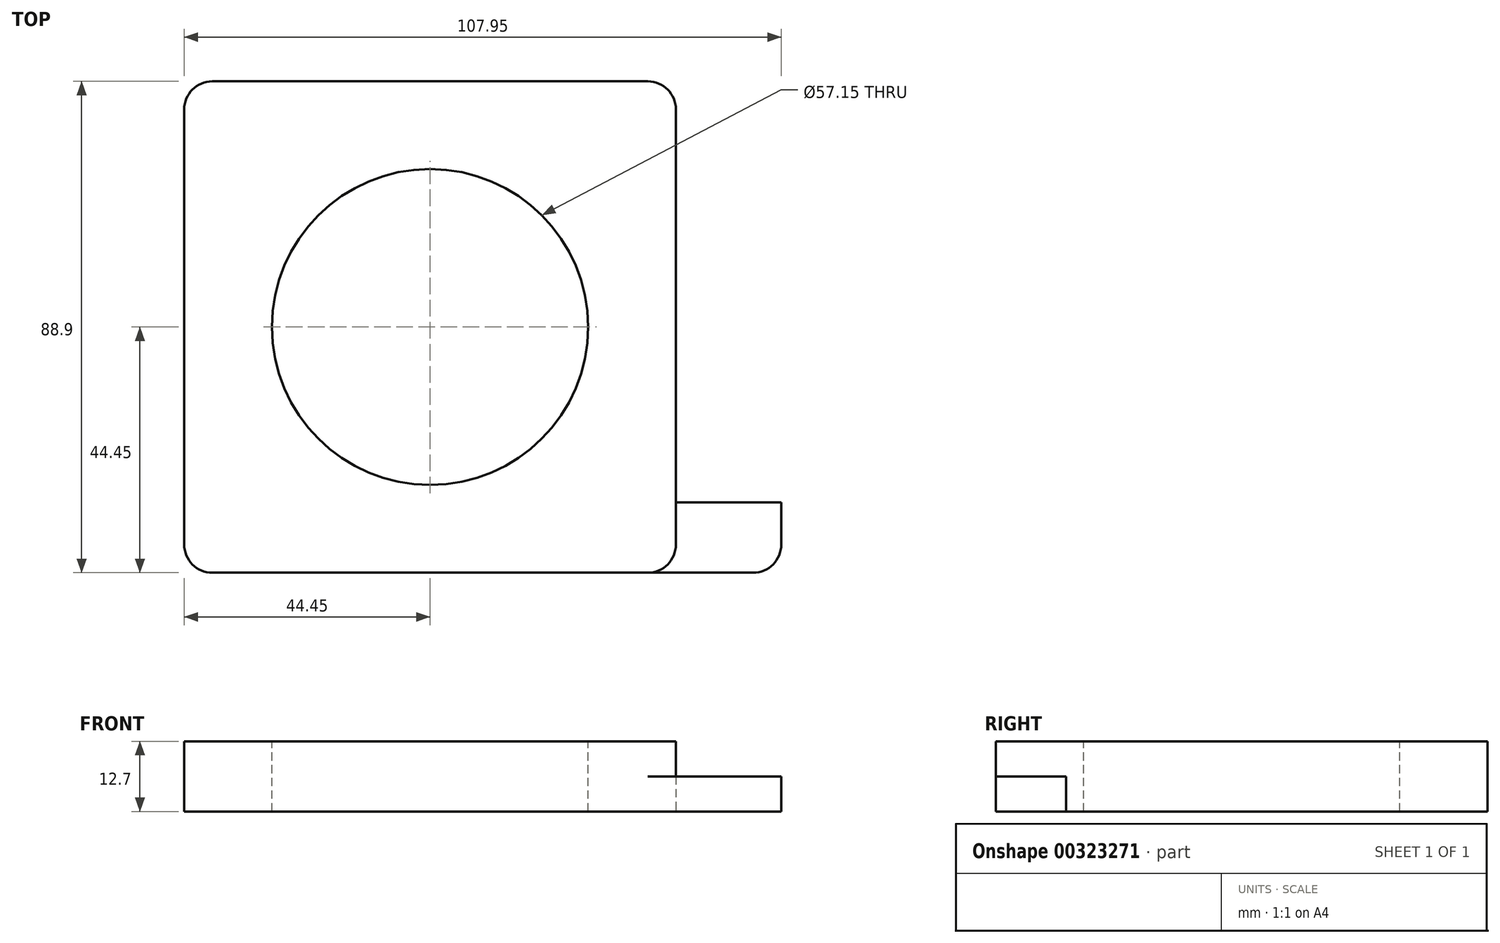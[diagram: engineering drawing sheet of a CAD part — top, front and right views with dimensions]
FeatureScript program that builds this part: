
annotation { "Feature Type Name" : "Feature", "Feature Type Description" : "" }
export const myFeature = defineFeature(function(context is Context, id is Id, definition is map)
    precondition{}
    {
        {
            var Q0;
            Q0=qCreatedBy(makeId("Top.planeOp"),FACE);
            var sketch = newSketch(context, id + "F0", { "sketchPlane" : qUnion([Q0])});
            skLineSegment(sketch, "E0.bottom", {"start": v(-44.45, 44.45) * mm, "end": v(44.45, 44.45) * mm});
            skLineSegment(sketch, "E0.top", {"start": v(-44.45, -44.45) * mm, "end": v(44.45, -44.45) * mm});
            skLineSegment(sketch, "E0.left", {"start": v(-44.45, 44.45) * mm, "end": v(-44.45, -44.45) * mm});
            skLineSegment(sketch, "E0.right", {"start": v(44.45, 44.45) * mm, "end": v(44.45, -44.45) * mm});
            skPoint(sketch, "E0.middle", {"position": v(0, 0) * mm});
            skLineSegment(sketch, "E1.bottom", {"start": v(44.45, -44.45) * mm, "end": v(63.5, -44.45) * mm});
            skLineSegment(sketch, "E1.top", {"start": v(44.45, -31.75) * mm, "end": v(63.5, -31.75) * mm});
            skLineSegment(sketch, "E1.left", {"start": v(44.45, -44.45) * mm, "end": v(44.45, -31.75) * mm});
            skLineSegment(sketch, "E1.right", {"start": v(63.5, -44.45) * mm, "end": v(63.5, -31.75) * mm});
            skSolve(sketch);
        }
        {
            var Q0;
            Q0=makeQuery(id+"F0.imprint","IMPRINT",FACE,{"disambiguationData":[TD([[makeQuery(id+"F0.imprint","IMPRINT",EDGE,{"derivedFrom":sQuery(id+"F0.wireOp",EDGE,"E0.bottom")}),-1.0]])]});
            extrude(context, id + "F1", {"entities" : qUnion([Q0]), "depth" : 12.7 * mm});
        }
        {
            var Q0;
            Q0=makeQuery(id+"F0.imprint","IMPRINT",FACE,{"disambiguationData":[TD([[makeQuery(id+"F0.imprint","IMPRINT",EDGE,{"derivedFrom":sQuery(id+"F0.wireOp",EDGE,"E1.bottom")}),1.0]])]});
            extrude(context, id + "F2", {"entities" : qUnion([Q0]), "operationType" : NewBodyOperationType.ADD, "depth" : 6.35 * mm});
        }
        {
            var Q0;
            Q0=makeQuery(id+"F1.opExtrude","SWEPT_EDGE",EDGE,{"disambiguationData":[OSD([sQuery(id+"F0.wireOp",EDGE,"E0.top"),sQuery(id+"F0.wireOp",EDGE,"E0.left")])]});
            var Q1;
            Q1=makeQuery(id+"F1.opExtrude","SWEPT_EDGE",EDGE,{"disambiguationData":[OSD([sQuery(id+"F0.wireOp",EDGE,"E0.bottom"),sQuery(id+"F0.wireOp",EDGE,"E0.left")])]});
            var Q2;
            Q2=makeQuery(id+"F1.opExtrude","SWEPT_EDGE",EDGE,{"disambiguationData":[OSD([sQuery(id+"F0.wireOp",EDGE,"E0.bottom"),sQuery(id+"F0.wireOp",EDGE,"E0.right")])]});
            var Q3;
            Q3=makeQuery(id+"F2.opExtrude","SWEPT_EDGE",EDGE,{"disambiguationData":[OSD([sQuery(id+"F0.wireOp",EDGE,"E0.right"),sQuery(id+"F0.wireOp",EDGE,"E1.top"),sQuery(id+"F0.wireOp",EDGE,"E1.left")])]});
            fillet(context, id + "F3", {"entities" : qUnion([Q0, Q1, Q2, Q3]), "radius" : 5.08 * mm, "tangentPropagation" : true, "allowEdgeOverflow" : false});
        }
        {
            var Q0;
            Q0=makeQuery(id+"F1.opExtrude","SWEPT_EDGE",EDGE,{"disambiguationData":[OSD([sQuery(id+"F0.wireOp",EDGE,"E0.top"),sQuery(id+"F0.wireOp",EDGE,"E1.bottom"),sQuery(id+"F0.wireOp",EDGE,"E1.left")])]});
            var Q1;
            Q1=makeQuery(id+"F2.opExtrude","SWEPT_EDGE",EDGE,{"disambiguationData":[OSD([sQuery(id+"F0.wireOp",EDGE,"E1.bottom"),sQuery(id+"F0.wireOp",EDGE,"E1.right")])]});
            fillet(context, id + "F4", {"entities" : qUnion([Q0, Q1]), "radius" : 5.08 * mm, "tangentPropagation" : true, "allowEdgeOverflow" : false});
        }
        {
            var Q0;
            Q0=makeQuery(id+"F1.opExtrude","CAP_FACE",FACE,{"disambiguationData":[OSD([sQuery(id+"F0.wireOp",EDGE,"E0.bottom"),sQuery(id+"F0.wireOp",EDGE,"E0.top"),sQuery(id+"F0.wireOp",EDGE,"E0.left"),sQuery(id+"F0.wireOp",EDGE,"E0.right"),sQuery(id+"F0.wireOp",EDGE,"E1.left")])],"isStart":false});
            var sketch = newSketch(context, id + "F5", { "sketchPlane" : qUnion([Q0])});
            skCircle(sketch, "E2", {"center": v(0, 0) * mm, "radius": 28.58 * mm});
            skSolve(sketch);
        }
        {
            var Q0;
            Q0=makeQuery(id+"F5.imprint","IMPRINT",FACE,{"disambiguationData":[TD([[makeQuery(id+"F5.imprint","IMPRINT",EDGE,{"derivedFrom":sQuery(id+"F5.wireOp",EDGE,"E2")}),1.0]])]});
            extrude(context, id + "F6", {"entities" : qUnion([Q0]), "operationType" : NewBodyOperationType.REMOVE, "oppositeDirection" : true, "depth" : 25.4 * mm});
        }
    });
